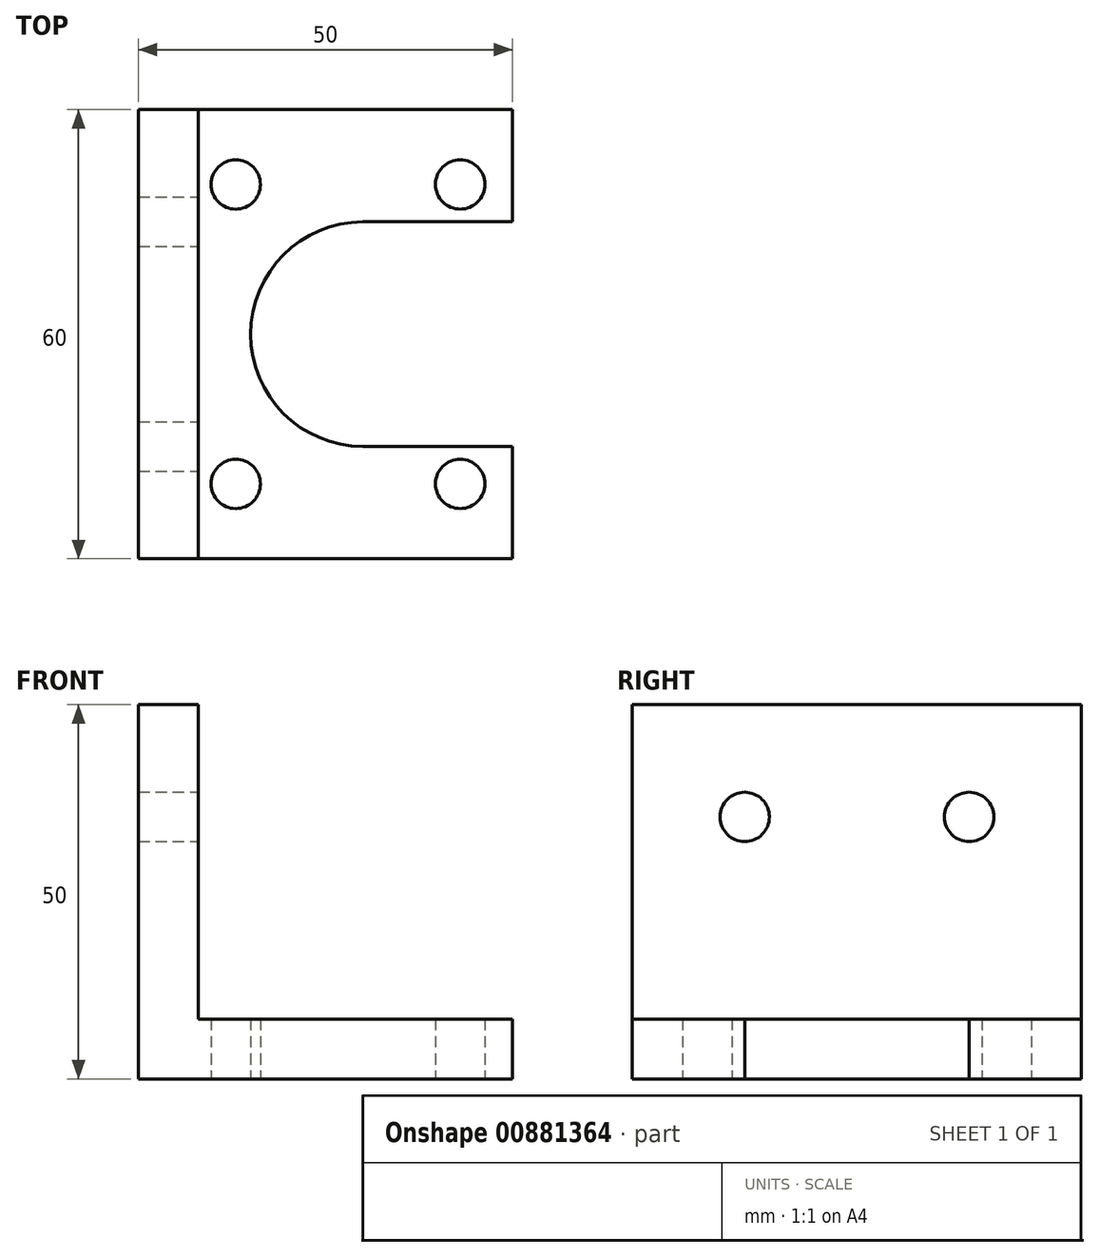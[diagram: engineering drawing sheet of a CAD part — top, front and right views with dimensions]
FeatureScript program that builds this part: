
annotation { "Feature Type Name" : "Feature", "Feature Type Description" : "" }
export const myFeature = defineFeature(function(context is Context, id is Id, definition is map)
    precondition{}
    {
        {
            var Q0;
            Q0=qCreatedBy(makeId("Top.planeOp"),FACE);
            var sketch = newSketch(context, id + "F0", { "sketchPlane" : qUnion([Q0])});
            skLineSegment(sketch, "E0.bottom", {"start": v(25, -30) * mm, "end": v(-25, -30) * mm});
            skLineSegment(sketch, "E0.top", {"start": v(25, 30) * mm, "end": v(-25, 30) * mm});
            skLineSegment(sketch, "E0.left", {"start": v(25, -30) * mm, "end": v(25, 30) * mm});
            skLineSegment(sketch, "E0.right", {"start": v(-25, -30) * mm, "end": v(-25, 30) * mm});
            skPoint(sketch, "E0.middle", {"position": v(0, 0) * mm});
            skCircle(sketch, "E1", {"center": v(5, 0) * mm, "radius": 15 * mm});
            skLineSegment(sketch, "E2", {"start": v(5, 15) * mm, "end": v(25, 15) * mm});
            skLineSegment(sketch, "E3", {"start": v(5, -15) * mm, "end": v(25, -15) * mm});
            skLineSegment(sketch, "E4", {"start": v(-17, 30) * mm, "end": v(-17, -30) * mm});
            skLineSegment(sketch, "E5.bottom", {"start": v(-12, 20) * mm, "end": v(18, 20) * mm, "construction": true});
            skLineSegment(sketch, "E5.top", {"start": v(-12, -20) * mm, "end": v(18, -20) * mm, "construction": true});
            skLineSegment(sketch, "E5.left", {"start": v(-12, 20) * mm, "end": v(-12, -20) * mm, "construction": true});
            skLineSegment(sketch, "E5.right", {"start": v(18, 20) * mm, "end": v(18, -20) * mm, "construction": true});
            skSolve(sketch);
        }
        {
            var Q0;
            {var subQ3=sQuery(id+"F0.wireOp",EDGE,"E2");Q0=makeQuery(id+"F0.imprint","IMPRINT",FACE,{"disambiguationData":[TD([[makeQuery(id+"F0.imprint","IMPRINT",EDGE,{"derivedFrom":subQ3}),1.0]])]});}
            extrude(context, id + "F1", {"entities" : qUnion([Q0]), "depth" : 8 * mm, "offsetDistance" : 25 * mm});
        }
        {
            var Q0;
            {var subQ0=sQuery(id+"F0.wireOp",EDGE,"E0.right");Q0=makeQuery(id+"F0.imprint","IMPRINT",FACE,{"disambiguationData":[TD([[makeQuery(id+"F0.imprint","IMPRINT",EDGE,{"derivedFrom":subQ0}),-1.0]])]});}
            extrude(context, id + "F2", {"entities" : qUnion([Q0]), "operationType" : NewBodyOperationType.ADD, "depth" : 50 * mm, "offsetDistance" : 25 * mm});
        }
        {
            var Q0;
            Q0=makeQuery(id+"F2.opExtrude","SWEPT_FACE",FACE,{"disambiguationData":[OSD([sQuery(id+"F0.wireOp",EDGE,"E4")])]});
            var sketch = newSketch(context, id + "F3", { "sketchPlane" : qUnion([Q0])});
            skLineSegment(sketch, "E6", {"start": v(-15, 35) * mm, "end": v(15, 35) * mm});
            skSolve(sketch);
        }
        {
            var Q0;
            Q0=sQuery(id+"F0.wireOp",VERTEX,"E5.top.end");
            var Q1;
            Q1=sQuery(id+"F0.wireOp",VERTEX,"E5.top.start");
            var Q2;
            Q2=sQuery(id+"F0.wireOp",VERTEX,"E5.bottom.end");
            var Q3;
            Q3=sQuery(id+"F0.wireOp",VERTEX,"E5.bottom.start");
            var Q4;
            Q4=makeQuery(id+"F1.opExtrude","SWEPT_BODY",BODY,{"disambiguationData":[OSD([sQuery(id+"F0.wireOp",EDGE,"E0.bottom"),sQuery(id+"F0.wireOp",EDGE,"E0.top"),sQuery(id+"F0.wireOp",EDGE,"E0.left"),sQuery(id+"F0.wireOp",EDGE,"E1"),sQuery(id+"F0.wireOp",EDGE,"E2"),sQuery(id+"F0.wireOp",EDGE,"E3"),sQuery(id+"F0.wireOp",EDGE,"E4")])]});
            hole(context, id + "F4", {"style" : HoleStyle.SIMPLE, "endStyle" : HoleEndStyle.BLIND, "oppositeDirection" : true, "standardTappedOrClearance" : lookupTablePath({ "fit" : "Normal", "standard" : "ISO", "size" : "M6", "type" : "Clearance" }), "standardBlindInLast" : lookupTablePath({ "fit" : "Normal", "standard" : "ISO", "size" : "M6", "type" : "Clearance" }), "holeDiameter" : 6.6 * mm, "majorDiameter" : 6 * mm, "holeDepth" : 17.25 * mm, "tappedDepth" : 15 * mm, "tapClearance" : 3, "startFromSketch" : true, "locations" : qUnion([Q0, Q1, Q2, Q3]), "scope" : qUnion([Q4])});
        }
        {
            var Q0;
            Q0=sQuery(id+"F3.wireOp",VERTEX,"E6.start");
            var Q1;
            Q1=sQuery(id+"F3.wireOp",VERTEX,"E6.end");
            var Q2;
            Q2=makeQuery(id+"F1.opExtrude","SWEPT_BODY",BODY,{"disambiguationData":[OSD([sQuery(id+"F0.wireOp",EDGE,"E0.bottom"),sQuery(id+"F0.wireOp",EDGE,"E0.top"),sQuery(id+"F0.wireOp",EDGE,"E0.left"),sQuery(id+"F0.wireOp",EDGE,"E1"),sQuery(id+"F0.wireOp",EDGE,"E2"),sQuery(id+"F0.wireOp",EDGE,"E3"),sQuery(id+"F0.wireOp",EDGE,"E4")])]});
            hole(context, id + "F5", {"style" : HoleStyle.SIMPLE, "endStyle" : HoleEndStyle.BLIND, "standardTappedOrClearance" : lookupTablePath({ "fit" : "Normal", "standard" : "ISO", "size" : "M6", "type" : "Clearance" }), "standardBlindInLast" : lookupTablePath({ "fit" : "Normal", "standard" : "ISO", "size" : "M6", "type" : "Clearance" }), "holeDiameter" : 6.6 * mm, "majorDiameter" : 5 * mm, "holeDepth" : 17.25 * mm, "tappedDepth" : 15 * mm, "tapClearance" : 3, "startFromSketch" : true, "locations" : qUnion([Q0, Q1]), "scope" : qUnion([Q2])});
        }
    });
